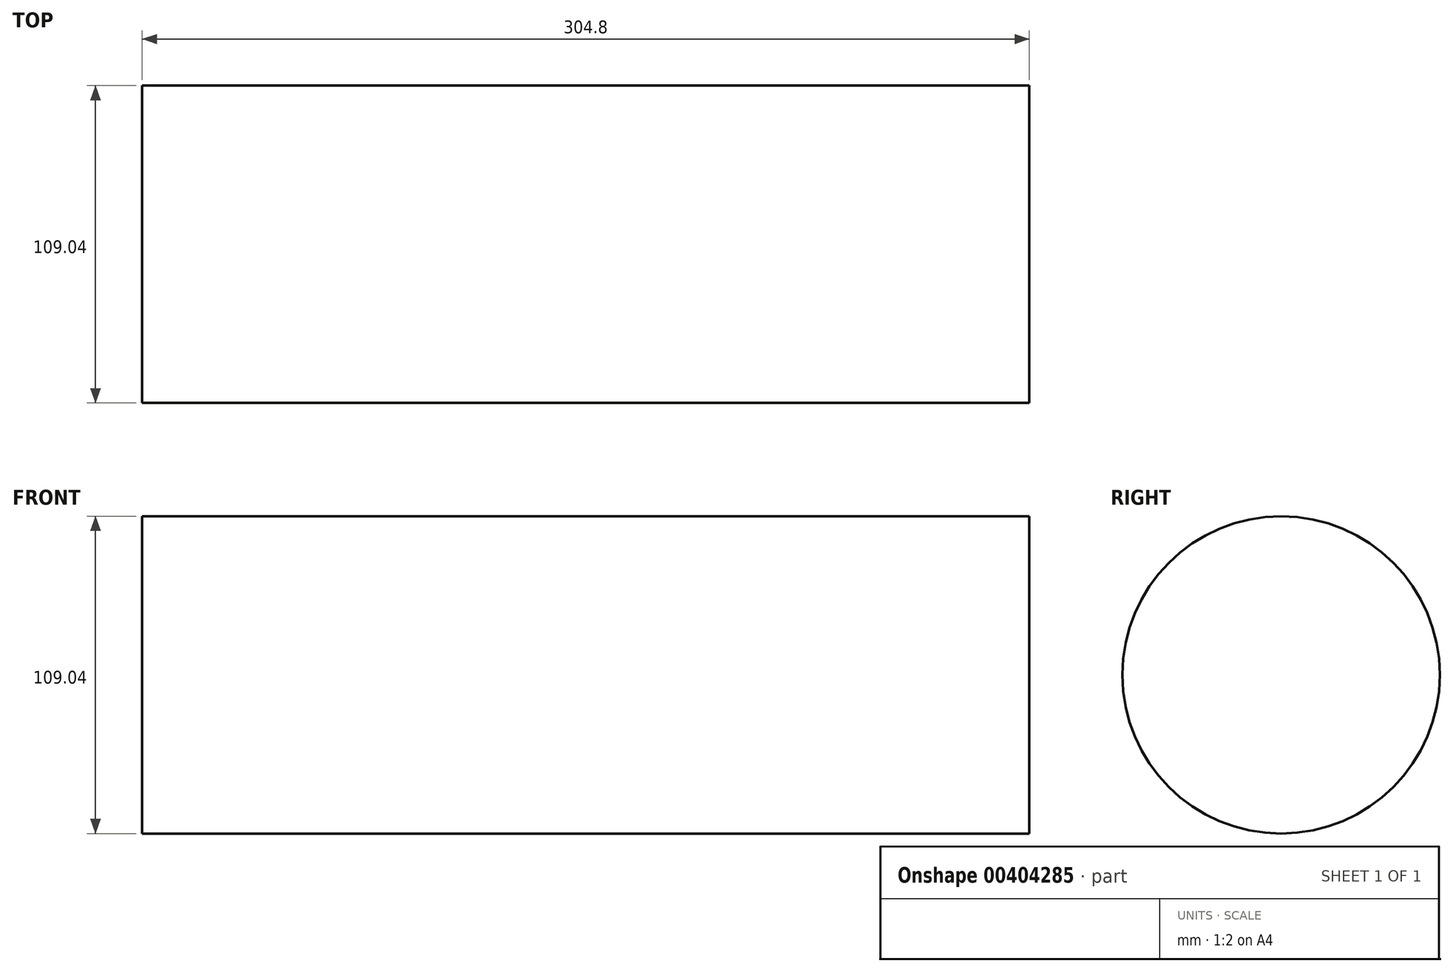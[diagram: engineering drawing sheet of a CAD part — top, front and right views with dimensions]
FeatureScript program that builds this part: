
annotation { "Feature Type Name" : "Feature", "Feature Type Description" : "" }
export const myFeature = defineFeature(function(context is Context, id is Id, definition is map)
    precondition{}
    {
        {
            var Q0;
            Q0=qCreatedBy(makeId("Right.planeOp"),FACE);
            var sketch = newSketch(context, id + "F0", { "sketchPlane" : qUnion([Q0])});
            skCircle(sketch, "E0", {"center": v(0, 0) * mm, "radius": 54.52 * mm});
            skSolve(sketch);
        }
        {
            var Q0;
            Q0=makeQuery(id+"F0.imprint","IMPRINT",FACE,{"disambiguationData":[TD([[makeQuery(id+"F0.imprint","IMPRINT",EDGE,{"derivedFrom":sQuery(id+"F0.wireOp",EDGE,"E0")}),1.0]])]});
            extrude(context, id + "F1", {"entities" : qUnion([Q0]), "depth" : 304.8 * mm});
        }
    });
